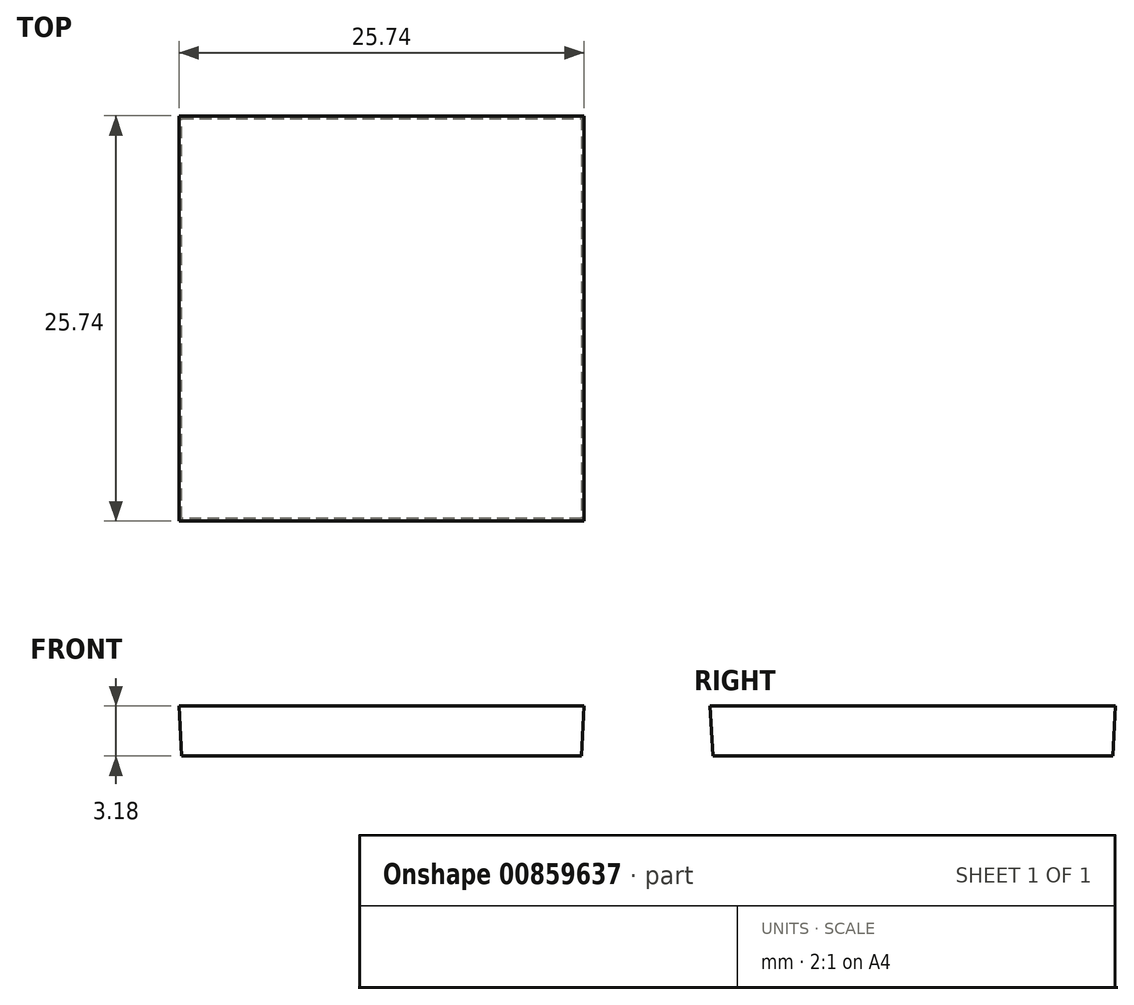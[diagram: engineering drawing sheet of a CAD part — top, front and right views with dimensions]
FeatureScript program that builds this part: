
annotation { "Feature Type Name" : "Feature", "Feature Type Description" : "" }
export const myFeature = defineFeature(function(context is Context, id is Id, definition is map)
    precondition{}
    {
        {
            var Q0;
            Q0=qCreatedBy(makeId("Top.planeOp"),FACE);
            var sketch = newSketch(context, id + "F0", { "sketchPlane" : qUnion([Q0])});
            skLineSegment(sketch, "E0.bottom", {"start": v(-12.7, 12.7) * mm, "end": v(12.7, 12.7) * mm});
            skLineSegment(sketch, "E0.top", {"start": v(-12.7, -12.7) * mm, "end": v(12.7, -12.7) * mm});
            skLineSegment(sketch, "E0.left", {"start": v(-12.7, 12.7) * mm, "end": v(-12.7, -12.7) * mm});
            skLineSegment(sketch, "E0.right", {"start": v(12.7, 12.7) * mm, "end": v(12.7, -12.7) * mm});
            skPoint(sketch, "E0.middle", {"position": v(0, 0) * mm});
            skSolve(sketch);
        }
        {
            var Q0;
            Q0=makeQuery(id+"F0.imprint","IMPRINT",FACE,{"disambiguationData":[TD([[makeQuery(id+"F0.imprint","IMPRINT",EDGE,{"derivedFrom":sQuery(id+"F0.wireOp",EDGE,"E0.bottom")}),-1.0]])]});
            extrude(context, id + "F1", {"entities" : qUnion([Q0]), "depth" : 3.17 * mm, "offsetDistance" : 25.4 * mm, "hasDraft" : true, "draftAngle" : 3 * degree});
        }
    });
